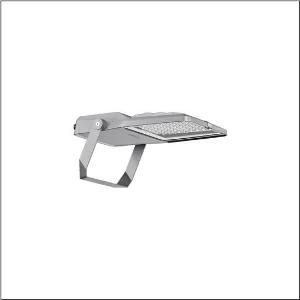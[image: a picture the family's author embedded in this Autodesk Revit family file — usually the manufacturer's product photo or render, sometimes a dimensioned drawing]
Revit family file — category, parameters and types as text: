
# Revit family: floodlight_fl_21_iq_mini___pl43_5xa7772d4a1a_cd74
name_source: partatom
category: Lighting Fixtures
units: mm (PartAtom-declared; Revit-internal decimal feet)

## family parameters
Cut with Voids When Loaded = No
Host = Face
Light Source = No
Part Type = Normal
Room Calculation Point = No
Round Connector Dimension = Use Diameter
Shared = No

## types (1)
- --- (1 x LED, 19090 lm, 143 W, 4000K)
    Apparent Load = 143 VA
    CIE Flux Codes = 27 78 99 100 100
    Color Rendering = 70
    Color Temperature = 4000K
    Default Elevation = 1800 mm
    Description = Floodlight FL 21 iQ mini, floodlight, primary light control with lens, of PMMA, primary optical cover: protective disc, of toughened safety glass, transparent, light distribution: PL43, light emission: direct distribution, installation type: surface-mounted, LED, High Power LED, rated luminous flux: 19.090lm, luminous efficacy: 134lm/W, light colour: 740, colour temperature: 4000K, control: Street-Remote, Auto-Match, Temp-Guard, Night-Set, Smart-Wire, Desk-Remote (wireless, voltage-free reading and setting of iQ features in the workshop via application-optimized NFC function/RFID function), optimised constant luminous flux control (CLO 2.0), with terminal, 6-pole, mains connection: 220..240V, AC, 50/60Hz, start of lifetime: 143W, end of service life: 152W, reduction: 61W, luminaire housing, of diecast aluminium, powder-coated, Siteco® metallic grey (DB 702S), corrosivity category C5 mid according to DIN EN ISO 12944, sealing non-destructively replaceable, mounting bracket, of steel, galvanised, powder-coated, Siteco® metallic grey (DB 702S), protection rating (complete): IP66, insulation class (complete): insulation class II (safety insulation), certification: CE, ENEC, VDE, protection symbol: D, impact resistance: IK08, permissible operating ambient temperature: -40..+40°C, permissible operating ambient temperature for outdoor applications: -40..+50°C, standard: DIN EN 12944, LABS conformity tested according to VDMA 24364:2018-05, packaging unit: 1 piece

Light Distribution: PL43
    Height = 70 mm
    Lamp = 1 x LED
    Lamp Light Flux = 19090 lm
    Lamp Power = 143 W
    Lamp count = 1
    Length = 485 mm
    Luminous efficacy = 133 lm/W
    Manufacturer = Siteco
    ModVariant = No
    Model = 5XA7772D4A1A
    Number of Poles = 1
    OnlyDefault = Yes
    Power Factor = 1
    Product Name = Floodlight FL 21 iQ mini | PL43
    Product group = floodlight | pylon annexe
    ProductGroupID = 6200
    Protection Class = Protection class II
    Protection Degree = IP 66
    RLX_Detail_Level = 1
    RLX_Emergency_Light_Flux = 0 lm
    RLX_Emergency_Type = 0
    RLX_Emergency_Type_DB = No
    RlxData = <blob elided: 96537 chars, md5=4e669b75>
    Socket = socket
    Standby Power = 0 W
    System Light Flux = 19090 lm
    System Power = 143 W
    Type Comments = factory setting: luminous flux: 100 % | dim-lin: 254 | 730 mA
    Type Image = l_1006845.jpg
    URL = http://relux.com
    VarID = @adj_111511
    Voltage = 0 V
    Weight = 0.00 kg
    Width = 337 mm

## geometry (parser evidence)
native form markers: Blend x4, Sweep x12
no freeform markers — native parametric forms only
